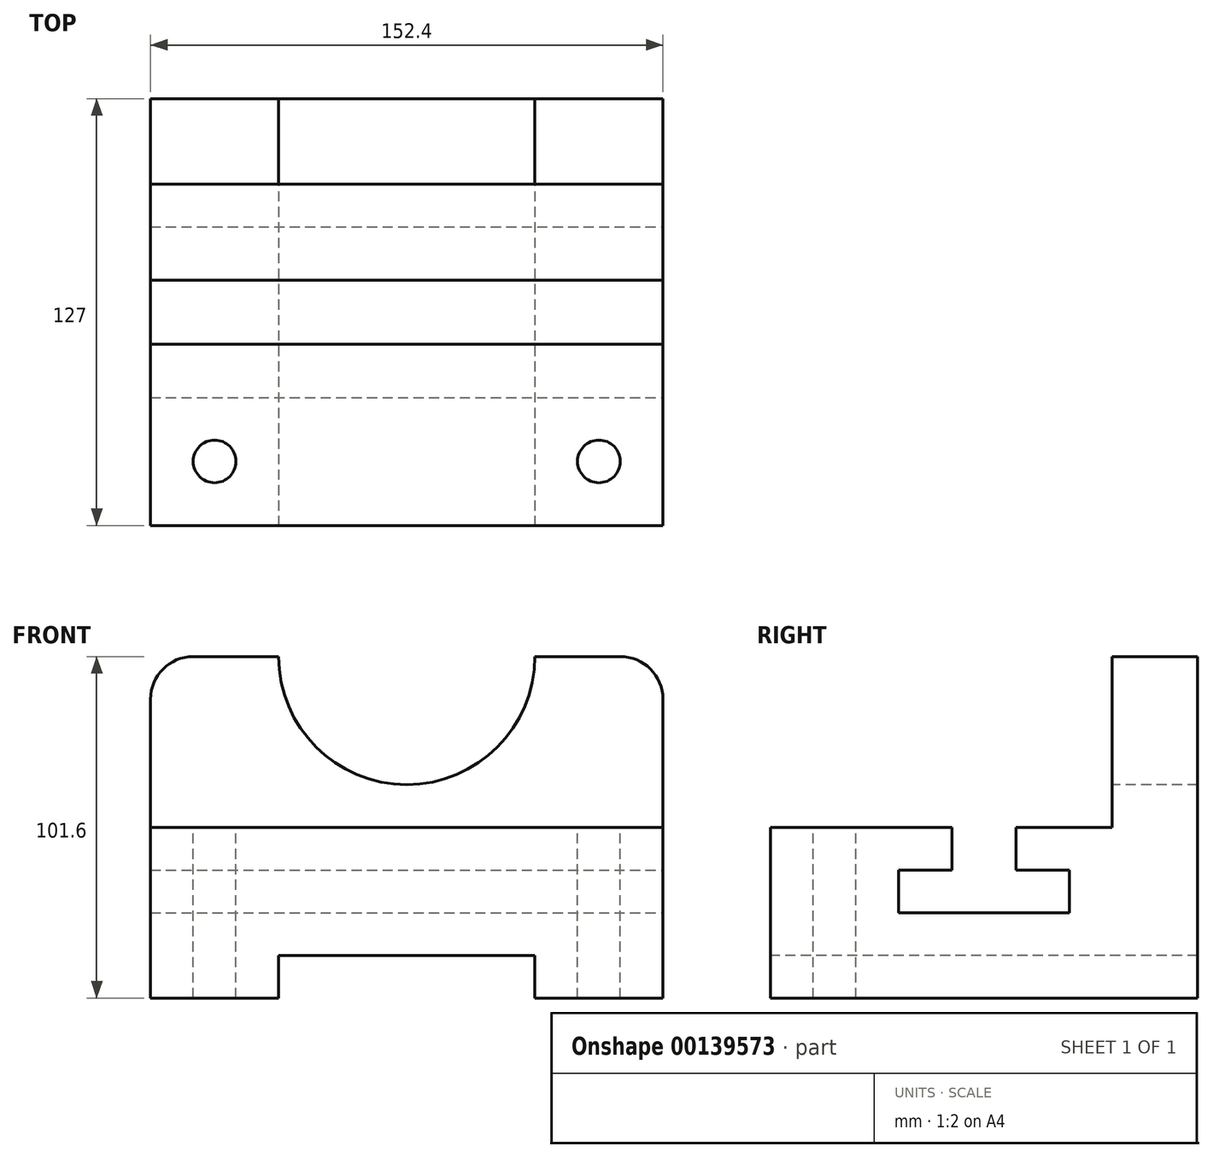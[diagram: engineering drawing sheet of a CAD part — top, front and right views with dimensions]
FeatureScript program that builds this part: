
annotation { "Feature Type Name" : "Feature", "Feature Type Description" : "" }
export const myFeature = defineFeature(function(context is Context, id is Id, definition is map)
    precondition{}
    {
        {
            var Q0;
            Q0=qCreatedBy(makeId("Right.planeOp"),FACE);
            var sketch = newSketch(context, id + "F0", { "sketchPlane" : qUnion([Q0])});
            skLineSegment(sketch, "E0", {"start": v(0, -25.4) * mm, "end": v(0, 25.4) * mm});
            skLineSegment(sketch, "E1", {"start": v(0, 25.4) * mm, "end": v(127, 25.4) * mm});
            skLineSegment(sketch, "E2", {"start": v(127, 25.4) * mm, "end": v(127, -25.4) * mm});
            skLineSegment(sketch, "E3", {"start": v(127, -25.4) * mm, "end": v(0, -25.4) * mm});
            skLineSegment(sketch, "E4", {"start": v(101.6, 25.4) * mm, "end": v(101.6, 76.2) * mm});
            skLineSegment(sketch, "E5", {"start": v(101.6, 76.2) * mm, "end": v(127, 76.2) * mm});
            skLineSegment(sketch, "E6", {"start": v(127, 25.4) * mm, "end": v(127, 76.2) * mm});
            skSolve(sketch);
        }
        {
            var Q0;
            Q0 = qSketchRegion(id + "F0", true);
            extrude(context, id + "F1", {"entities" : qUnion([Q0]), "oppositeDirection" : true, "depth" : 152.4 * mm});
        }
        {
            var Q0;
            Q0=makeQuery(id+"F1.opExtrude","CAP_FACE",FACE,{"disambiguationData":[OSD([sQuery(id+"F0.wireOp",EDGE,"E0"),sQuery(id+"F0.wireOp",EDGE,"E1"),sQuery(id+"F0.wireOp",EDGE,"E2"),sQuery(id+"F0.wireOp",EDGE,"E3"),sQuery(id+"F0.wireOp",EDGE,"E4"),sQuery(id+"F0.wireOp",EDGE,"E5"),sQuery(id+"F0.wireOp",EDGE,"E6")])],"isStart":true});
            var sketch = newSketch(context, id + "F2", { "sketchPlane" : qUnion([Q0])});
            skLineSegment(sketch, "E7", {"start": v(53.97, 25.4) * mm, "end": v(53.97, 12.7) * mm});
            skLineSegment(sketch, "E8", {"start": v(53.98, 12.7) * mm, "end": v(38.1, 12.7) * mm});
            skLineSegment(sketch, "E9", {"start": v(38.1, 12.7) * mm, "end": v(38.1, 0) * mm});
            skLineSegment(sketch, "E10", {"start": v(38.1, 0) * mm, "end": v(88.9, 0) * mm});
            skLineSegment(sketch, "E11", {"start": v(88.9, 0) * mm, "end": v(88.9, 12.7) * mm});
            skLineSegment(sketch, "E12", {"start": v(88.9, 12.7) * mm, "end": v(73.03, 12.7) * mm});
            skLineSegment(sketch, "E13", {"start": v(73.03, 12.7) * mm, "end": v(73.03, 25.4) * mm});
            skSolve(sketch);
        }
        {
            var Q0;
            Q0 = qSketchRegion(id + "F2", true);
            var Q1;
            {var subQ0=sQuery(id+"F2.wireOp",EDGE,"E7");Q1=makeQuery(id+"F2.imprint","IMPRINT",FACE,{"disambiguationData":[TD([[makeQuery(id+"F2.imprint","IMPRINT",EDGE,{"derivedFrom":subQ0}),1.0]])]});}
            extrude(context, id + "F3", {"entities" : qUnion([Q0, Q1]), "operationType" : NewBodyOperationType.REMOVE, "oppositeDirection" : true, "depth" : 152.4 * mm});
        }
        {
            var Q0;
            Q0=makeQuery(id+"F1.opExtrude","SWEPT_FACE",FACE,{"disambiguationData":[OSD([sQuery(id+"F0.wireOp",EDGE,"E0")])]});
            var sketch = newSketch(context, id + "F4", { "sketchPlane" : qUnion([Q0])});
            skLineSegment(sketch, "E14", {"start": v(-114.3, -25.4) * mm, "end": v(-114.3, -12.7) * mm});
            skLineSegment(sketch, "E15", {"start": v(-114.3, -12.7) * mm, "end": v(-38.1, -12.7) * mm});
            skLineSegment(sketch, "E16", {"start": v(-38.1, -12.7) * mm, "end": v(-38.1, -25.4) * mm});
            skSolve(sketch);
        }
        {
            var Q0;
            {var subQ0=sQuery(id+"F4.wireOp",EDGE,"E14");Q0=makeQuery(id+"F4.imprint","IMPRINT",FACE,{"disambiguationData":[TD([[makeQuery(id+"F4.imprint","IMPRINT",EDGE,{"derivedFrom":subQ0}),-1.0]])]});}
            extrude(context, id + "F5", {"entities" : qUnion([Q0]), "operationType" : NewBodyOperationType.REMOVE, "oppositeDirection" : true, "depth" : 127 * mm});
        }
        {
            var Q0;
            Q0=makeQuery(id+"F1.opExtrude","SWEPT_FACE",FACE,{"disambiguationData":[OSD([sQuery(id+"F0.wireOp",EDGE,"E4")])]});
            var sketch = newSketch(context, id + "F6", { "sketchPlane" : qUnion([Q0])});
            skArc(sketch, "E17", {"start": v(-114.3, 76.2) * mm, "mid": v(-76.2, 38.1) * mm, "end": v(-38.1, 76.2) * mm});
            skLineSegment(sketch, "E18", {"start": v(-114.3, 76.2) * mm, "end": v(-38.1, 76.2) * mm});
            skSolve(sketch);
        }
        {
            var Q0;
            Q0=makeQuery(id+"F6.imprint","IMPRINT",FACE,{"disambiguationData":[TD([[makeQuery(id+"F6.imprint","IMPRINT",EDGE,{"derivedFrom":sQuery(id+"F6.wireOp",EDGE,"E17")}),1.0]])]});
            extrude(context, id + "F7", {"entities" : qUnion([Q0]), "operationType" : NewBodyOperationType.REMOVE, "oppositeDirection" : true, "depth" : 25.4 * mm});
        }
        {
            var Q0;
            Q0=makeQuery(id+"F1.opExtrude","CAP_EDGE",EDGE,{"disambiguationData":[OSD([sQuery(id+"F0.wireOp",EDGE,"E5")])],"isStart":false});
            var Q1;
            Q1=makeQuery(id+"F1.opExtrude","CAP_EDGE",EDGE,{"disambiguationData":[OSD([sQuery(id+"F0.wireOp",EDGE,"E5")])],"isStart":true});
            fillet(context, id + "F8", {"entities" : qUnion([Q0, Q1]), "radius" : 12.7 * mm, "tangentPropagation" : true, "allowEdgeOverflow" : false});
        }
        {
            var Q0;
            {var subQ0=sQuery(id+"F0.wireOp",EDGE,"E0");var subQ6=sQuery(id+"F0.wireOp",EDGE,"E1");Q0=makeQuery(id+"F3.boolean.opBoolean","SPLIT",FACE,{"disambiguationData":[TD([makeQuery(id+"F1.opExtrude","SWEPT_FACE",FACE,{"disambiguationData":[OSD([subQ0])]})])],"derivedFrom":makeQuery(id+"F1.opExtrude","SWEPT_FACE",FACE,{"disambiguationData":[OSD([subQ6])]})});}
            var sketch = newSketch(context, id + "F9", { "sketchPlane" : qUnion([Q0])});
            skCircle(sketch, "E19", {"center": v(-133.35, 19.05) * mm, "radius": 6.35 * mm});
            skCircle(sketch, "E20", {"center": v(-19.05, 19.05) * mm, "radius": 6.35 * mm});
            skSolve(sketch);
        }
        {
            var Q0;
            Q0 = qSketchRegion(id + "F9", true);
            extrude(context, id + "F10", {"entities" : qUnion([Q0]), "operationType" : NewBodyOperationType.REMOVE, "oppositeDirection" : true, "depth" : 50.8 * mm});
        }
    });
